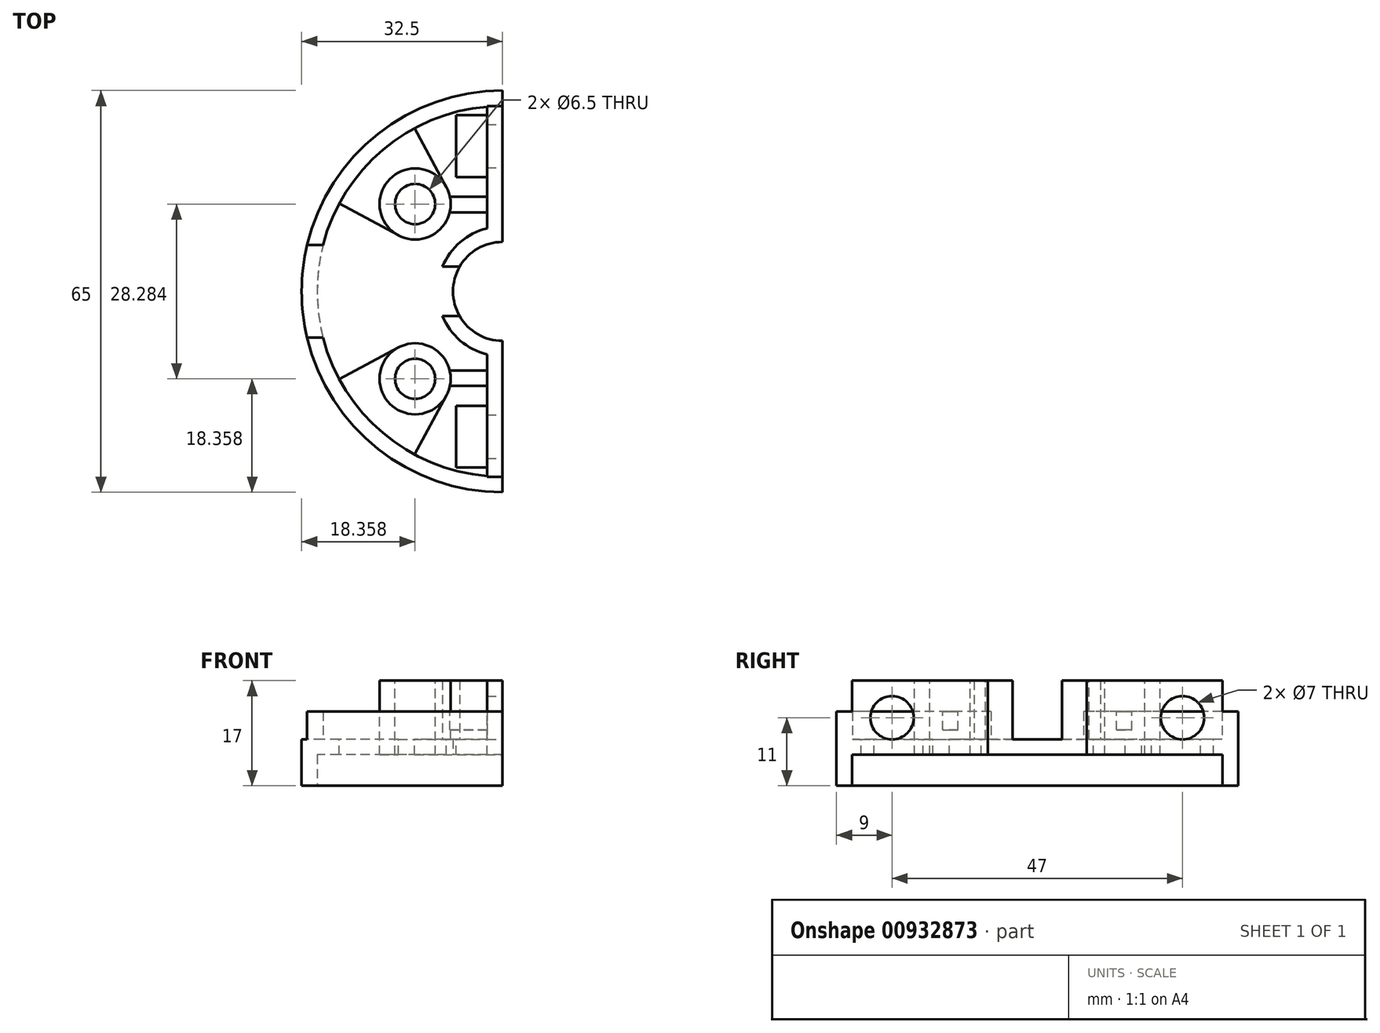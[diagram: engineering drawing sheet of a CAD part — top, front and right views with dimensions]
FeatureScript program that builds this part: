
annotation { "Feature Type Name" : "Feature", "Feature Type Description" : "" }
export const myFeature = defineFeature(function(context is Context, id is Id, definition is map)
    precondition{}
    {
        {
            var Q0;
            Q0=qCreatedBy(makeId("Top.planeOp"),FACE);
            var sketch = newSketch(context, id + "F0", { "sketchPlane" : qUnion([Q0])});
            skCircle(sketch, "E0", {"center": v(0, 0) * mm, "radius": 32.5 * mm});
            skSolve(sketch);
        }
        {
            var Q0;
            Q0=qSketchRegion(id+"F0",true);
            extrude(context, id + "F1", {"entities" : qUnion([Q0]), "depth" : 12 * mm, "offsetDistance" : 25 * mm});
        }
        {
            var Q0;
            Q0=qCreatedBy(makeId("Top.planeOp"),FACE);
            var sketch = newSketch(context, id + "F2", { "sketchPlane" : qUnion([Q0])});
            skCircle(sketch, "E1", {"center": v(0, 0) * mm, "radius": 8 * mm});
            skSolve(sketch);
        }
        {
            var Q0;
            Q0=qSketchRegion(id+"F2",true);
            extrude(context, id + "F3", {"entities" : qUnion([Q0]), "operationType" : NewBodyOperationType.REMOVE, "depth" : 25 * mm, "offsetDistance" : 25 * mm});
        }
        {
            var Q0;
            Q0=makeQuery(id+"F1.opExtrude","CAP_FACE",FACE,{"disambiguationData":[OSD([sQuery(id+"F0.wireOp",EDGE,"E0")])],"isStart":false});
            var sketch = newSketch(context, id + "F4", { "sketchPlane" : qUnion([Q0])});
            skCircle(sketch, "E2", {"center": v(-14.14, 14.14) * mm, "radius": 3.25 * mm});
            skCircle(sketch, "E3.MirrorC", {"center": v(-14.14, -14.14) * mm, "radius": 3.25 * mm});
            skCircle(sketch, "E4.MirrorC", {"center": v(14.14, 14.14) * mm, "radius": 3.25 * mm});
            skCircle(sketch, "E5.MirrorC", {"center": v(14.14, -14.14) * mm, "radius": 3.25 * mm});
            skSolve(sketch);
        }
        {
            var Q0;
            Q0=qSketchRegion(id+"F4",true);
            extrude(context, id + "F5", {"entities" : qUnion([Q0]), "operationType" : NewBodyOperationType.REMOVE, "oppositeDirection" : true, "depth" : 25 * mm, "offsetDistance" : 25 * mm});
        }
        {
            var Q0;
            Q0=makeQuery(id+"F1.opExtrude","CAP_FACE",FACE,{"disambiguationData":[OSD([sQuery(id+"F0.wireOp",EDGE,"E0")])],"isStart":false});
            shell(context, id + "F6", {"entities" : qUnion([Q0]), "thickness" : 2.5 * mm});
        }
        {
            var Q0;
            {var subQ0=sQuery(id+"F0.wireOp",EDGE,"E0");Q0=makeQuery(id+"F6.opShell","OFFSET_FACE",FACE,{"disambiguationData":[OSD([subQ0]),TDD([makeQuery(id+"F1.opExtrude","CAP_FACE",FACE,{"disambiguationData":[OSD([subQ0])],"isStart":true})])]});}
            var sketch = newSketch(context, id + "F7", { "sketchPlane" : qUnion([Q0])});
            skLineSegment(sketch, "E6", {"start": v(16.87, 9.08) * mm, "end": v(26.42, 14.22) * mm});
            skLineSegment(sketch, "E7", {"start": v(9.08, 16.87) * mm, "end": v(14.22, 26.42) * mm});
            skLineSegment(sketch, "E8.MirrorCS", {"start": v(-9.08, 16.87) * mm, "end": v(-14.22, 26.42) * mm});
            skLineSegment(sketch, "E9.MirrorCS", {"start": v(-16.87, 9.08) * mm, "end": v(-26.42, 14.22) * mm});
            skLineSegment(sketch, "E10.MirrorCS", {"start": v(16.87, -9.08) * mm, "end": v(26.42, -14.22) * mm});
            skLineSegment(sketch, "E11.MirrorCS", {"start": v(9.08, -16.87) * mm, "end": v(14.22, -26.42) * mm});
            skLineSegment(sketch, "E12.MirrorCS", {"start": v(-16.87, -9.08) * mm, "end": v(-26.42, -14.22) * mm});
            skLineSegment(sketch, "E13.MirrorCS", {"start": v(-9.08, -16.87) * mm, "end": v(-14.22, -26.42) * mm});
            skSolve(sketch);
        }
        {
            var Q0;
            Q0=qSketchRegion(id+"F7",true);
            var Q1;
            {var subQ0=sQuery(id+"F7.wireOp",EDGE,"E6");Q1=makeQuery(id+"F7.imprint","IMPRINT",FACE,{"disambiguationData":[TD([[makeQuery(id+"F7.imprint","IMPRINT",EDGE,{"derivedFrom":subQ0}),1.0]])]});}
            var Q2;
            {var subQ0=sQuery(id+"F7.wireOp",EDGE,"E8.MirrorCS");Q2=makeQuery(id+"F7.imprint","IMPRINT",FACE,{"disambiguationData":[TD([[makeQuery(id+"F7.imprint","IMPRINT",EDGE,{"derivedFrom":subQ0}),1.0]])]});}
            var Q3;
            {var subQ0=sQuery(id+"F7.wireOp",EDGE,"E10.MirrorCS");Q3=makeQuery(id+"F7.imprint","IMPRINT",FACE,{"disambiguationData":[TD([[makeQuery(id+"F7.imprint","IMPRINT",EDGE,{"derivedFrom":subQ0}),-1.0]])]});}
            var Q4;
            {var subQ0=sQuery(id+"F7.wireOp",EDGE,"E12.MirrorCS");Q4=makeQuery(id+"F7.imprint","IMPRINT",FACE,{"disambiguationData":[TD([[makeQuery(id+"F7.imprint","IMPRINT",EDGE,{"derivedFrom":subQ0}),1.0]])]});}
            extrude(context, id + "F8", {"entities" : qUnion([Q0, Q1, Q2, Q3, Q4]), "operationType" : NewBodyOperationType.REMOVE, "oppositeDirection" : true, "depth" : 25 * mm, "offsetDistance" : 25 * mm});
        }
        {
            var Q0;
            Q0=qCreatedBy(makeId("Top.planeOp"),FACE);
            var sketch = newSketch(context, id + "F9", { "sketchPlane" : qUnion([Q0])});
            skLineSegment(sketch, "E14.bottom", {"start": v(0, 49.33) * mm, "end": v(37.18, 49.33) * mm});
            skLineSegment(sketch, "E14.top", {"start": v(0, -45) * mm, "end": v(37.18, -45) * mm});
            skLineSegment(sketch, "E14.left", {"start": v(0, 49.33) * mm, "end": v(0, -45) * mm});
            skLineSegment(sketch, "E14.right", {"start": v(37.18, 49.33) * mm, "end": v(37.18, -45) * mm});
            skSolve(sketch);
        }
        {
            var Q0;
            Q0 = qSketchRegion(id + "F9", true);
            extrude(context, id + "F10", {"entities" : qUnion([Q0]), "operationType" : NewBodyOperationType.REMOVE, "depth" : 25 * mm, "offsetDistance" : 25 * mm});
        }
        {
            var Q0;
            Q0=qCreatedBy(makeId("Right.planeOp"),FACE);
            var sketch = newSketch(context, id + "F11", { "sketchPlane" : qUnion([Q0])});
            skLineSegment(sketch, "E15.bottom", {"start": v(4, 2.5) * mm, "end": v(-4, 2.5) * mm});
            skLineSegment(sketch, "E15.top", {"start": v(4, 12) * mm, "end": v(-4, 12) * mm});
            skLineSegment(sketch, "E15.left", {"start": v(4, 2.5) * mm, "end": v(4, 12) * mm});
            skLineSegment(sketch, "E15.right", {"start": v(-4, 2.5) * mm, "end": v(-4, 12) * mm});
            skSolve(sketch);
        }
        {
            var Q0;
            Q0 = qSketchRegion(id + "F11", true);
            extrude(context, id + "F12", {"entities" : qUnion([Q0]), "operationType" : NewBodyOperationType.REMOVE, "oppositeDirection" : true, "depth" : 10.5 * mm, "offsetDistance" : 25 * mm});
        }
        {
            var Q0;
            Q0=qCreatedBy(makeId("Right.planeOp"),FACE);
            cPlane(context, id + "F13", {"entities" : qUnion([Q0]), "cplaneType" : CPlaneType.OFFSET, "offset" : 32.5 * mm, "oppositeDirection" : true, "width" : 150 * mm, "height" : 150 * mm});
        }
        {
            var Q0;
            Q0=qCreatedBy(id+"F13.planeOp",FACE);
            var sketch = newSketch(context, id + "F14", { "sketchPlane" : qUnion([Q0])});
            skLineSegment(sketch, "E16.bottom", {"start": v(7.5, 12) * mm, "end": v(-7.5, 12) * mm});
            skLineSegment(sketch, "E16.top", {"start": v(7.5, 2.5) * mm, "end": v(-7.5, 2.5) * mm});
            skLineSegment(sketch, "E16.left", {"start": v(7.5, 12) * mm, "end": v(7.5, 2.5) * mm});
            skLineSegment(sketch, "E16.right", {"start": v(-7.5, 12) * mm, "end": v(-7.5, 2.5) * mm});
            skSolve(sketch);
        }
        {
            var Q0;
            Q0 = qSketchRegion(id + "F14", true);
            extrude(context, id + "F15", {"entities" : qUnion([Q0]), "operationType" : NewBodyOperationType.REMOVE, "depth" : 5 * mm, "offsetDistance" : 25 * mm});
        }
        {
            var Q0;
            Q0=makeQuery(id+"F1.opExtrude","CAP_FACE",FACE,{"disambiguationData":[OSD([sQuery(id+"F0.wireOp",EDGE,"E0")])],"isStart":true});
            var sketch = newSketch(context, id + "F16", { "sketchPlane" : qUnion([Q0])});
            skArc(sketch, "E17", {"start": v(0, 30) * mm, "mid": v(-30, 0) * mm, "end": v(0, -30) * mm});
            skArc(sketch, "E18", {"start": v(0, 32.5) * mm, "mid": v(-32.5, 0) * mm, "end": v(0, -32.5) * mm});
            skLineSegment(sketch, "E19", {"start": v(0, -32.5) * mm, "end": v(0, -30) * mm});
            skLineSegment(sketch, "E20", {"start": v(0, 32.5) * mm, "end": v(0, 30) * mm});
            skSolve(sketch);
        }
        {
            var Q0;
            {var subQ0=sQuery(id+"F0.wireOp",EDGE,"E0");Q0=makeQuery(id+"F6.opShell","OFFSET_FACE",FACE,{"disambiguationData":[OSD([subQ0]),TDD([makeQuery(id+"F1.opExtrude","CAP_FACE",FACE,{"disambiguationData":[OSD([subQ0])],"isStart":false})]),OD(2.0)]});}
            extrude(context, id + "F17", {"entities" : qUnion([Q0]), "operationType" : NewBodyOperationType.REMOVE, "oppositeDirection" : true, "depth" : 5 * mm, "offsetDistance" : 25 * mm});
        }
        {
            var Q0;
            Q0=makeQuery(id+"F1.opExtrude","CAP_FACE",FACE,{"disambiguationData":[OSD([sQuery(id+"F0.wireOp",EDGE,"E0")])],"isStart":false});
            extrude(context, id + "F18", {"entities" : qUnion([Q0]), "operationType" : NewBodyOperationType.REMOVE, "oppositeDirection" : true, "depth" : 5 * mm, "offsetDistance" : 25 * mm});
        }
        {
            var Q0;
            {var subQ15=makeQuery(id+"F3.boolean.opBoolean","COPY",EDGE,{"derivedFrom":makeQuery(id+"F3.opExtrude","CAP_EDGE",EDGE,{"disambiguationData":[OSD([sQuery(id+"F2.wireOp",EDGE,"E1")])],"isStart":true})});Q0=makeQuery(id+"F16.imprint","IMPRINT",FACE,{"disambiguationData":[TD([[makeQuery(id+"F16.imprint","IMPRINT",EDGE,{"derivedFrom":subQ15}),1.0]])]});}
            var Q1;
            Q1=makeQuery(id+"F16.imprint","IMPRINT",FACE,{"disambiguationData":[TD([[makeQuery(id+"F16.imprint","IMPRINT",EDGE,{"derivedFrom":sQuery(id+"F16.wireOp",EDGE,"E18")}),-1.0]])]});
            extrude(context, id + "F19", {"entities" : qUnion([Q0, Q1]), "operationType" : NewBodyOperationType.ADD, "depth" : 5 * mm, "offsetDistance" : 25 * mm});
        }
        {
            var Q0;
            Q0=makeQuery(id+"F19.opExtrude","CAP_FACE",FACE,{"disambiguationData":[OSD([sQuery(id+"F0.wireOp",EDGE,"E0"),sQuery(id+"F2.wireOp",EDGE,"E1"),sQuery(id+"F4.wireOp",EDGE,"E2"),sQuery(id+"F4.wireOp",EDGE,"E3.MirrorC"),sQuery(id+"F7.wireOp",EDGE,"E8.MirrorCS"),sQuery(id+"F7.wireOp",EDGE,"E9.MirrorCS"),sQuery(id+"F7.wireOp",EDGE,"E12.MirrorCS"),sQuery(id+"F7.wireOp",EDGE,"E13.MirrorCS"),sQuery(id+"F9.wireOp",EDGE,"E14.left"),sQuery(id+"F16.wireOp",EDGE,"E17"),sQuery(id+"F16.wireOp",EDGE,"E18"),sQuery(id+"F16.wireOp",EDGE,"E19"),sQuery(id+"F16.wireOp",EDGE,"E20")])],"isStart":false});
            var sketch = newSketch(context, id + "F20", { "sketchPlane" : qUnion([Q0])});
            skLineSegment(sketch, "E21", {"start": v(-26.42, 14.22) * mm, "end": v(-14.22, 26.42) * mm});
            skLineSegment(sketch, "E22", {"start": v(-14.22, 26.42) * mm, "end": v(-2.02, 14.22) * mm});
            skLineSegment(sketch, "E23", {"start": v(-2.02, 14.22) * mm, "end": v(-14.22, 2.02) * mm});
            skLineSegment(sketch, "E24", {"start": v(-14.22, 2.02) * mm, "end": v(-26.42, 14.22) * mm});
            skLineSegment(sketch, "E25.MirrorCS", {"start": v(-14.22, -2.02) * mm, "end": v(-26.42, -14.22) * mm});
            skLineSegment(sketch, "E26.MirrorCS", {"start": v(-26.42, -14.22) * mm, "end": v(-14.22, -26.42) * mm});
            skLineSegment(sketch, "E27.MirrorCS", {"start": v(-14.22, -26.42) * mm, "end": v(-2.02, -14.22) * mm});
            skLineSegment(sketch, "E28.MirrorCS", {"start": v(-2.02, -14.22) * mm, "end": v(-14.22, -2.02) * mm});
            skSolve(sketch);
        }
        {
            var Q0;
            Q0 = qSketchRegion(id + "F20", true);
            extrude(context, id + "F21", {"entities" : qUnion([Q0]), "operationType" : NewBodyOperationType.REMOVE, "oppositeDirection" : true, "depth" : 5 * mm, "offsetDistance" : 25 * mm});
        }
        {
            var Q0;
            Q0=makeQuery(id+"F17.boolean.opBoolean","COPY",FACE,{"derivedFrom":makeQuery(id+"F17.opExtrude","CAP_FACE",FACE,{"disambiguationData":[OSD([sQuery(id+"F0.wireOp",EDGE,"E0")])],"isStart":false})});
            var sketch = newSketch(context, id + "F22", { "sketchPlane" : qUnion([Q0])});
            skLineSegment(sketch, "E29", {"start": v(-8.5, -15.3) * mm, "end": v(0, -15.3) * mm});
            skLineSegment(sketch, "E30", {"start": v(0, -15.3) * mm, "end": v(0, -12.8) * mm});
            skLineSegment(sketch, "E31", {"start": v(0, -12.8) * mm, "end": v(-8.55, -12.8) * mm});
            skLineSegment(sketch, "E32.MirrorCS", {"start": v(0, 12.8) * mm, "end": v(-8.55, 12.8) * mm});
            skLineSegment(sketch, "E33.MirrorCS", {"start": v(0, 15.3) * mm, "end": v(0, 12.8) * mm});
            skLineSegment(sketch, "E34.MirrorCS", {"start": v(-8.5, 15.3) * mm, "end": v(0, 15.3) * mm});
            skSolve(sketch);
        }
        {
            var Q0;
            {var subQ0=sQuery(id+"F22.wireOp",EDGE,"E29");Q0=makeQuery(id+"F22.imprint","IMPRINT",FACE,{"disambiguationData":[TD([[makeQuery(id+"F22.imprint","IMPRINT",EDGE,{"derivedFrom":subQ0}),1.0]])]});}
            extrude(context, id + "F23", {"entities" : qUnion([Q0]), "operationType" : NewBodyOperationType.ADD, "oppositeDirection" : true, "depth" : 3 * mm, "offsetDistance" : 25 * mm});
        }
        {
            var Q0;
            {var subQ0=sQuery(id+"F0.wireOp",EDGE,"E0");Q0=makeQuery(id+"F15.boolean.opBoolean","MERGE",FACE,{"derivedFrom":[makeQuery(id+"F12.boolean.opBoolean","MERGE",FACE,{"derivedFrom":[makeQuery(id+"F6.opShell","OFFSET_FACE",FACE,{"disambiguationData":[OSD([subQ0]),TDD([makeQuery(id+"F1.opExtrude","CAP_FACE",FACE,{"disambiguationData":[OSD([subQ0])],"isStart":true})])]})],"fromTools":[makeQuery(id+"F12.opExtrude","SWEPT_FACE",FACE,{"disambiguationData":[OSD([sQuery(id+"F11.wireOp",EDGE,"E15.bottom")])]})]})],"fromTools":[makeQuery(id+"F15.opExtrude","SWEPT_FACE",FACE,{"disambiguationData":[OSD([sQuery(id+"F14.wireOp",EDGE,"E16.top")])]})]});}
            var sketch = newSketch(context, id + "F24", { "sketchPlane" : qUnion([Q0])});
            skLineSegment(sketch, "E35.bottom", {"start": v(0, -30) * mm, "end": v(-2.5, -30) * mm});
            skLineSegment(sketch, "E35.top", {"start": v(0, -9.12) * mm, "end": v(-2.5, -9.12) * mm});
            skLineSegment(sketch, "E35.left", {"start": v(0, -30) * mm, "end": v(0, -9.12) * mm});
            skLineSegment(sketch, "E35.right", {"start": v(-2.5, -30) * mm, "end": v(-2.5, -9.12) * mm});
            skLineSegment(sketch, "E36.MirrorCS", {"start": v(0, 30) * mm, "end": v(0, 9.12) * mm});
            skLineSegment(sketch, "E37.MirrorCS", {"start": v(0, 30) * mm, "end": v(-2.5, 30) * mm});
            skLineSegment(sketch, "E38.MirrorCS", {"start": v(-2.5, 30) * mm, "end": v(-2.5, 9.12) * mm});
            skLineSegment(sketch, "E39.MirrorCS", {"start": v(0, 9.12) * mm, "end": v(-2.5, 9.12) * mm});
            skSolve(sketch);
        }
        {
            var Q0;
            Q0 = qSketchRegion(id + "F24", true);
            extrude(context, id + "F25", {"entities" : qUnion([Q0]), "operationType" : NewBodyOperationType.ADD, "depth" : 9.5 * mm, "offsetDistance" : 25 * mm});
        }
        {
            var Q0;
            {var subQ0=sQuery(id+"F9.wireOp",EDGE,"E14.left");Q0=makeQuery(id+"F25.boolean.opBoolean","MERGE",FACE,{"derivedFrom":[makeQuery(id+"F19.boolean.opBoolean","MERGE",FACE,{"derivedFrom":[makeQuery(id+"F10.boolean.opBoolean","COPY",FACE,{"disambiguationData":[OD(1.0)],"derivedFrom":makeQuery(id+"F10.opExtrude","SWEPT_FACE",FACE,{"disambiguationData":[OSD([subQ0])]})}),makeQuery(id+"F19.opExtrude","SWEPT_FACE",FACE,{"disambiguationData":[OSD([subQ0,sQuery(id+"F16.wireOp",EDGE,"E20")])]})]}),makeQuery(id+"F23.opExtrude","SWEPT_FACE",FACE,{"disambiguationData":[OSD([sQuery(id+"F22.wireOp",EDGE,"E30")])]}),makeQuery(id+"F25.opExtrude","SWEPT_FACE",FACE,{"disambiguationData":[OSD([sQuery(id+"F24.wireOp",EDGE,"E35.left")])]})]});}
            var sketch = newSketch(context, id + "F26", { "sketchPlane" : qUnion([Q0])});
            skCircle(sketch, "E40", {"center": v(-23.5, 6) * mm, "radius": 3.5 * mm});
            skCircle(sketch, "E41.MirrorC", {"center": v(23.5, 6) * mm, "radius": 3.5 * mm});
            skSolve(sketch);
        }
        {
            var Q0;
            Q0 = qSketchRegion(id + "F26", true);
            extrude(context, id + "F27", {"entities" : qUnion([Q0]), "operationType" : NewBodyOperationType.REMOVE, "oppositeDirection" : true, "depth" : 2.5 * mm, "offsetDistance" : 25 * mm});
        }
        {
            var Q0;
            {var subQ0=sQuery(id+"F0.wireOp",EDGE,"E0");Q0=makeQuery(id+"F15.boolean.opBoolean","MERGE",FACE,{"derivedFrom":[makeQuery(id+"F12.boolean.opBoolean","MERGE",FACE,{"derivedFrom":[makeQuery(id+"F6.opShell","OFFSET_FACE",FACE,{"disambiguationData":[OSD([subQ0]),TDD([makeQuery(id+"F1.opExtrude","CAP_FACE",FACE,{"disambiguationData":[OSD([subQ0])],"isStart":true})])]})],"fromTools":[makeQuery(id+"F12.opExtrude","SWEPT_FACE",FACE,{"disambiguationData":[OSD([sQuery(id+"F11.wireOp",EDGE,"E15.bottom")])]})]})],"fromTools":[makeQuery(id+"F15.opExtrude","SWEPT_FACE",FACE,{"disambiguationData":[OSD([sQuery(id+"F14.wireOp",EDGE,"E16.top")])]})]});}
            var sketch = newSketch(context, id + "F28", { "sketchPlane" : qUnion([Q0])});
            skLineSegment(sketch, "E42.bottom", {"start": v(-2.5, -28.5) * mm, "end": v(-7.5, -28.5) * mm});
            skLineSegment(sketch, "E42.top", {"start": v(-2.5, -18.5) * mm, "end": v(-7.5, -18.5) * mm});
            skLineSegment(sketch, "E42.left", {"start": v(-2.5, -28.5) * mm, "end": v(-2.5, -18.5) * mm});
            skLineSegment(sketch, "E42.right", {"start": v(-7.5, -28.5) * mm, "end": v(-7.5, -18.5) * mm});
            skLineSegment(sketch, "E43.MirrorCS", {"start": v(-2.5, 18.5) * mm, "end": v(-7.5, 18.5) * mm});
            skLineSegment(sketch, "E44.MirrorCS", {"start": v(-7.5, 28.5) * mm, "end": v(-7.5, 18.5) * mm});
            skLineSegment(sketch, "E45.MirrorCS", {"start": v(-2.5, 28.5) * mm, "end": v(-2.5, 18.5) * mm});
            skLineSegment(sketch, "E46.MirrorCS", {"start": v(-2.5, 28.5) * mm, "end": v(-7.5, 28.5) * mm});
            skSolve(sketch);
        }
        {
            var Q0;
            Q0 = qSketchRegion(id + "F28", true);
            extrude(context, id + "F29", {"entities" : qUnion([Q0]), "operationType" : NewBodyOperationType.REMOVE, "oppositeDirection" : true, "depth" : 2.5 * mm, "offsetDistance" : 25 * mm});
        }
        {
            var Q0;
            Q0=makeQuery(id+"F1.opExtrude","SWEPT_BODY",BODY,{"disambiguationData":[OSD([sQuery(id+"F0.wireOp",EDGE,"E0")])]});
            var Q1;
            Q1=qCreatedBy(makeId("Front.planeOp"),FACE);
            mirror(context, id + "F30", {"operationType" : NewBodyOperationType.ADD, "entities" : qUnion([Q0]), "mirrorPlane" : qUnion([Q1])});
        }
    });
